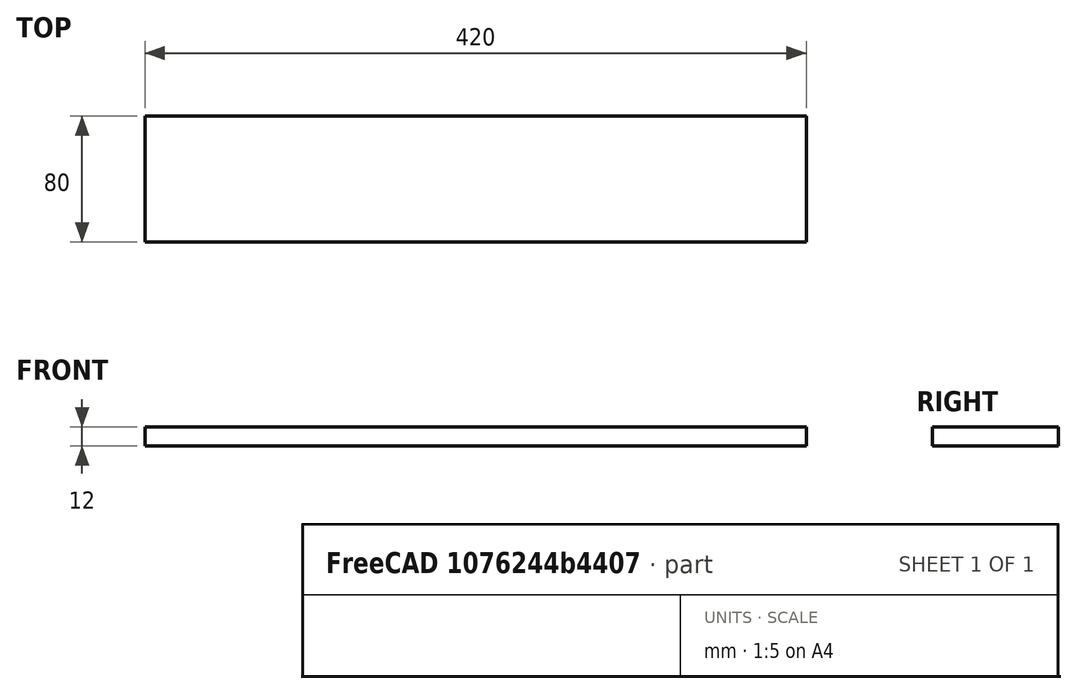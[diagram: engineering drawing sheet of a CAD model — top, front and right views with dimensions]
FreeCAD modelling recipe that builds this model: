
FCSTD DOCUMENT  (FreeCAD 0.18R16131 (Git))
Label: Front_plate
License: All rights reserved
LicenseURL: http://en.wikipedia.org/wiki/All_rights_reserved
objects: Sketcher::SketchObject×1, PartDesign::Pad×1, PartDesign::Body×1
note: 4 computed .brp shape members not serialized (recipe doc carries the construction recipe); baked Part::Feature solids carry a one-line shape summary decoded from their .brp

FEATURE [Sketcher::SketchObject] Sketch
  MapMode = 5
  Support = -> [XY_Plane]
  sketch-geometry (4):
    g0: LineSegment StartX=0 StartY=0 StartZ=0 EndX=420 EndY=0 EndZ=0
    g1: LineSegment StartX=420 StartY=0 StartZ=0 EndX=420 EndY=80 EndZ=0
    g2: LineSegment StartX=420 StartY=80 StartZ=0 EndX=0 EndY=80 EndZ=0
    g3: LineSegment StartX=0 StartY=80 StartZ=0 EndX=0 EndY=0 EndZ=0
  constraints (11):
    c: Coincident(g0,g1)
    c: Coincident(g1,g2)
    c: Coincident(g2,g3)
    c: Coincident(g3,g0)
    c: Horizontal(g0)
    c: Horizontal(g2)
    c: Vertical(g1)
    c: Vertical(g3)
    c: Coincident(g0,g-1)
    c: DistanceY(g3,g3) = 80
    c: DistanceX(g2,g2) = 420
FEATURE [PartDesign::Pad] Pad
  Length = 12
  Length2 = 100
  Profile = -> Sketch
  Type = 0
FEATURE [PartDesign::Body] Body
  Group = -> [Sketch,Pad]
  Origin = -> Origin
  Tip = -> Pad
